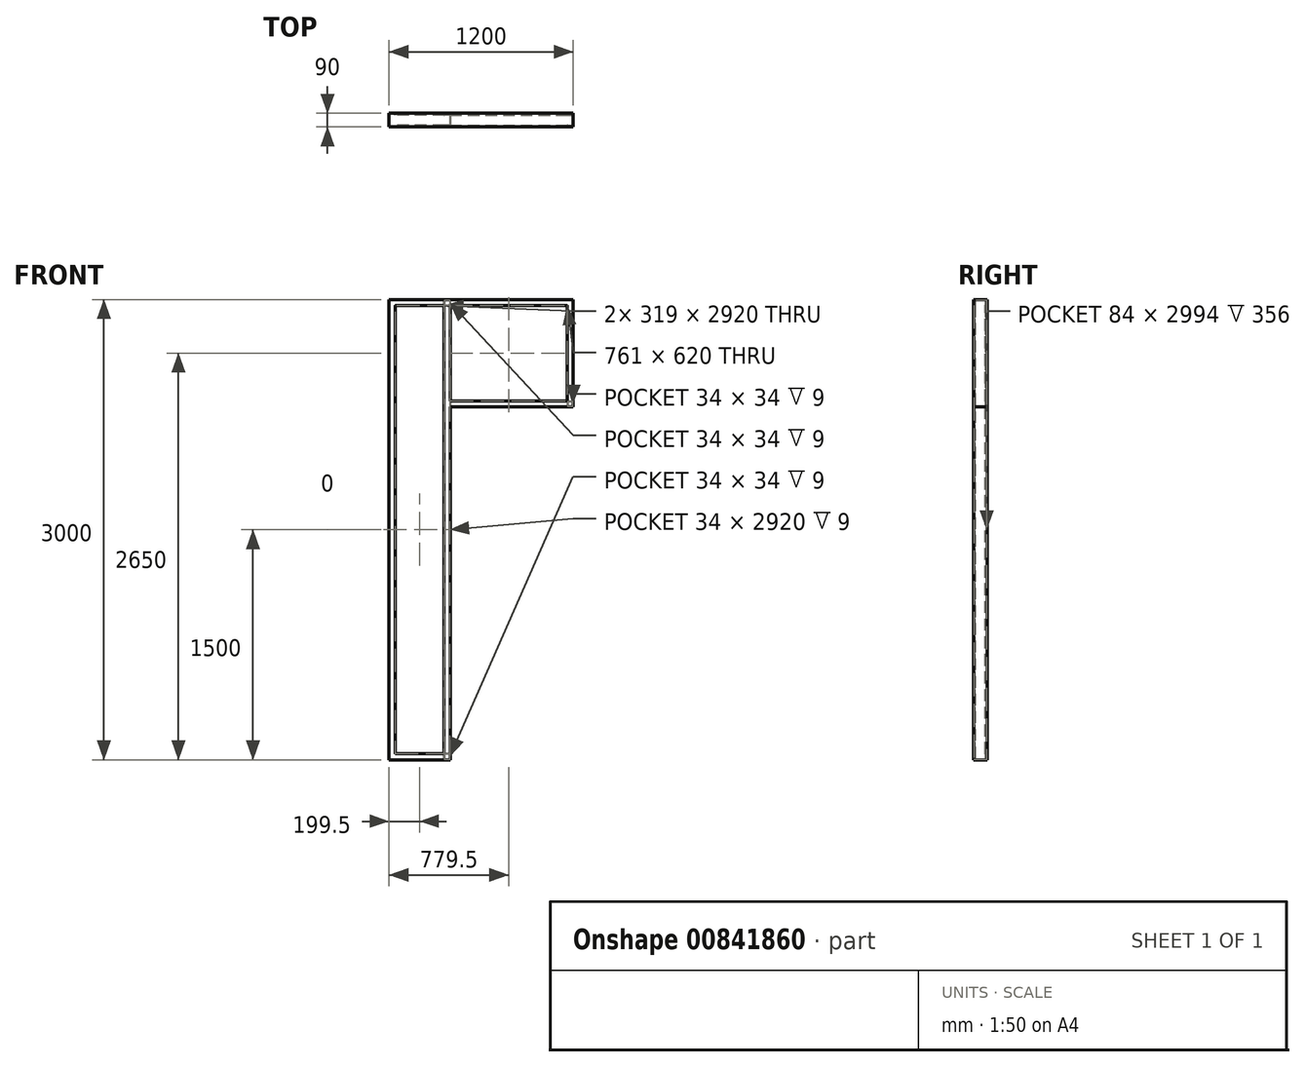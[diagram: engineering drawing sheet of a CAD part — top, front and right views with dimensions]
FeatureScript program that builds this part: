
annotation { "Feature Type Name" : "Feature", "Feature Type Description" : "" }
export const myFeature = defineFeature(function(context is Context, id is Id, definition is map)
    precondition{}
    {
        {
            var Q0;
            Q0=qCreatedBy(makeId("Front.planeOp"),FACE);
            var sketch = newSketch(context, id + "F0", { "sketchPlane" : qUnion([Q0])});
            skLineSegment(sketch, "E0.bottom", {"start": v(0, 0) * mm, "end": v(1200, 0) * mm});
            skLineSegment(sketch, "E0.top", {"start": v(0, 3000) * mm, "end": v(1200, 3000) * mm});
            skLineSegment(sketch, "E0.left", {"start": v(0, 0) * mm, "end": v(0, 3000) * mm});
            skLineSegment(sketch, "E0.right", {"start": v(1200, 0) * mm, "end": v(1200, 3000) * mm});
            skSolve(sketch);
        }
        {
            var Q0;
            Q0=qCreatedBy(makeId("Top.planeOp"),FACE);
            var sketch = newSketch(context, id + "F1", { "sketchPlane" : qUnion([Q0])});
            skLineSegment(sketch, "E1", {"start": v(0, 0) * mm, "end": v(0, -45) * mm});
            skLineSegment(sketch, "E2", {"start": v(0, -45) * mm, "end": v(40, -45) * mm});
            skLineSegment(sketch, "E3", {"start": v(40, -45) * mm, "end": v(40, -33) * mm});
            skLineSegment(sketch, "E4.MirrorCS", {"start": v(0, 0) * mm, "end": v(0, 45) * mm});
            skLineSegment(sketch, "E5.MirrorCS", {"start": v(0, 45) * mm, "end": v(40, 45) * mm});
            skLineSegment(sketch, "E6.MirrorCS", {"start": v(40, 45) * mm, "end": v(40, 33) * mm});
            skLineSegment(sketch, "E7.0", {"start": v(37, 42) * mm, "end": v(37, 33) * mm});
            skLineSegment(sketch, "E7.1", {"start": v(3, 42) * mm, "end": v(37, 42) * mm});
            skLineSegment(sketch, "E7.2", {"start": v(37, -42) * mm, "end": v(37, -33) * mm});
            skLineSegment(sketch, "E7.3", {"start": v(3, -42) * mm, "end": v(37, -42) * mm});
            skLineSegment(sketch, "E7.4", {"start": v(3, 0) * mm, "end": v(3, -42) * mm});
            skLineSegment(sketch, "E7.5", {"start": v(3, 0) * mm, "end": v(3, 42) * mm});
            skLineSegment(sketch, "E8", {"start": v(37, 33) * mm, "end": v(40, 33) * mm});
            skLineSegment(sketch, "E9", {"start": v(37, -33) * mm, "end": v(40, -33) * mm});
            skSolve(sketch);
        }
        {
            var Q0;
            Q0=qSketchRegion(id+"F1",true);
            var Q1;
            Q1=qConstructionFilter(qBodyType(qCreatedBy(id+"F0",EDGE),BodyType.WIRE),ConstructionObject.NO);
            sweep(context, id + "F2", {"profiles" : qUnion([Q0]), "path" : qUnion([Q1])});
        }
        {
            var Q0;
            Q0=qCreatedBy(makeId("Top.planeOp"),FACE);
            var sketch = newSketch(context, id + "F3", { "sketchPlane" : qUnion([Q0])});
            skLineSegment(sketch, "E10", {"start": v(359, -45) * mm, "end": v(399, -45) * mm});
            skLineSegment(sketch, "E11", {"start": v(399, -45) * mm, "end": v(399, 45) * mm});
            skLineSegment(sketch, "E12", {"start": v(399, 45) * mm, "end": v(359, 45) * mm});
            skLineSegment(sketch, "E13", {"start": v(359, 45) * mm, "end": v(359, 33) * mm});
            skLineSegment(sketch, "E14", {"start": v(359, -45) * mm, "end": v(359, -33) * mm});
            skLineSegment(sketch, "E15", {"start": v(400, -276.13) * mm, "end": v(400, 155.47) * mm, "construction": true});
            skLineSegment(sketch, "E16.0", {"start": v(1195, -40) * mm, "end": v(5, -40) * mm});
            skLineSegment(sketch, "E16.1", {"start": v(1195, 40) * mm, "end": v(1195, -40) * mm});
            skLineSegment(sketch, "E16.2", {"start": v(5, 40) * mm, "end": v(1195, 40) * mm});
            skLineSegment(sketch, "E16.3", {"start": v(5, 40) * mm, "end": v(5, -40) * mm});
            skLineSegment(sketch, "E17.0", {"start": v(362, 42) * mm, "end": v(362, 33) * mm});
            skLineSegment(sketch, "E17.1", {"start": v(362, -42) * mm, "end": v(362, -33) * mm});
            skLineSegment(sketch, "E17.2", {"start": v(362, -42) * mm, "end": v(396, -42) * mm});
            skLineSegment(sketch, "E17.3", {"start": v(396, -42) * mm, "end": v(396, 42) * mm});
            skLineSegment(sketch, "E17.4", {"start": v(396, 42) * mm, "end": v(362, 42) * mm});
            skLineSegment(sketch, "E18", {"start": v(362, -33) * mm, "end": v(359, -33) * mm});
            skLineSegment(sketch, "E19", {"start": v(362, 33) * mm, "end": v(359, 33) * mm});
            skSolve(sketch);
        }
        {
            var Q0;
            {var subQ1=sQuery(id+"F3.wireOp",EDGE,"E10");Q0=makeQuery(id+"F3.imprint","IMPRINT",FACE,{"disambiguationData":[TD([[makeQuery(id+"F3.imprint","IMPRINT",EDGE,{"derivedFrom":subQ1}),1.0]])]});}
            var Q1;
            {var subQ0=sQuery(id+"F3.wireOp",EDGE,"E16.0");var subQ1=sQuery(id+"F3.wireOp",EDGE,"E11");var subQ2=makeQuery(id+"F3.imprint","INTERSECT",VERTEX,{"derivedFrom":[subQ1,subQ0]});Q1=makeQuery(id+"F3.imprint","IMPRINT",FACE,{"disambiguationData":[TD([[makeQuery(id+"F3.imprint","IMPRINT",EDGE,{"disambiguationData":[TD([[subQ2,-1.0]])],"derivedFrom":subQ1}),1.0]])]});}
            var Q2;
            {var subQ0=sQuery(id+"F3.wireOp",EDGE,"E18");Q2=makeQuery(id+"F3.imprint","IMPRINT",FACE,{"disambiguationData":[TD([[makeQuery(id+"F3.imprint","IMPRINT",EDGE,{"derivedFrom":subQ0}),1.0]])]});}
            var Q3;
            {var subQ1=sQuery(id+"F3.wireOp",EDGE,"E12");Q3=makeQuery(id+"F3.imprint","IMPRINT",FACE,{"disambiguationData":[TD([[makeQuery(id+"F3.imprint","IMPRINT",EDGE,{"derivedFrom":subQ1}),1.0]])]});}
            var Q4;
            {var subQ0=sQuery(id+"F3.wireOp",EDGE,"E19");Q4=makeQuery(id+"F3.imprint","IMPRINT",FACE,{"disambiguationData":[TD([[makeQuery(id+"F3.imprint","IMPRINT",EDGE,{"derivedFrom":subQ0}),-1.0]])]});}
            var Q5;
            {var subQ0=sQuery(id+"F3.wireOp",EDGE,"fbeb7f0c-a459-400f-91ed-7fec257c8f050.MirrorCS");Q5=makeQuery(id+"F3.imprint","IMPRINT",FACE,{"disambiguationData":[TD([[makeQuery(id+"F3.imprint","IMPRINT",EDGE,{"derivedFrom":subQ0}),1.0]])]});}
            var Q6;
            {var subQ1=sQuery(id+"F3.wireOp",EDGE,"567eaf2c-da89-443f-b3b3-d68592a5250c0.MirrorCS");Q6=makeQuery(id+"F3.imprint","IMPRINT",FACE,{"disambiguationData":[TD([[makeQuery(id+"F3.imprint","IMPRINT",EDGE,{"derivedFrom":subQ1}),-1.0]])]});}
            var Q7;
            {var subQ0=sQuery(id+"F3.wireOp",EDGE,"E16.0");var subQ1=sQuery(id+"F3.wireOp",EDGE,"1e470031-5891-413e-a47c-f06d65b3e17f0.MirrorCS");var subQ2=makeQuery(id+"F3.imprint","INTERSECT",VERTEX,{"derivedFrom":[subQ1,subQ0]});Q7=makeQuery(id+"F3.imprint","IMPRINT",FACE,{"disambiguationData":[TD([[makeQuery(id+"F3.imprint","IMPRINT",EDGE,{"disambiguationData":[TD([[subQ2,-1.0]])],"derivedFrom":subQ1}),-1.0]])]});}
            var Q8;
            {var subQ5=sQuery(id+"F3.wireOp",EDGE,"ca9fbca5-8cf1-4a5b-8b27-837bc25230130.MirrorCS");Q8=makeQuery(id+"F3.imprint","IMPRINT",FACE,{"disambiguationData":[TD([[makeQuery(id+"F3.imprint","IMPRINT",EDGE,{"derivedFrom":subQ5}),-1.0]])]});}
            var Q9;
            {var subQ0=sQuery(id+"F3.wireOp",EDGE,"47aaed49-ff0d-4512-a623-d8c6419a6b470.MirrorCS");Q9=makeQuery(id+"F3.imprint","IMPRINT",FACE,{"disambiguationData":[TD([[makeQuery(id+"F3.imprint","IMPRINT",EDGE,{"derivedFrom":subQ0}),-1.0]])]});}
            var Q10;
            Q10=makeQuery(id+"F2.opSweep","SWEPT_FACE",FACE,{"disambiguationData":[OSD([sQuery(id+"F0.wireOp",EDGE,"E0.top"),sQuery(id+"F1.wireOp",EDGE,"E7.4"),sQuery(id+"F1.wireOp",EDGE,"E7.5")])]});
            extrude(context, id + "F4", {"entities" : qUnion([Q0, Q1, Q2, Q3, Q4, Q5, Q6, Q7, Q8, Q9]), "operationType" : NewBodyOperationType.ADD, "endBound" : BoundingType.UP_TO_SURFACE, "depth" : 25 * mm, "endBoundEntityFace" : qUnion([Q10]), "offsetDistance" : 25 * mm});
        }
        {
            var Q0;
            Q0=makeQuery(id+"F4.boolean.opBoolean","MERGE",FACE,{"derivedFrom":[makeQuery(id+"F2.opSweep","SWEPT_FACE",FACE,{"disambiguationData":[OSD([sQuery(id+"F0.wireOp",EDGE,"E0.left"),sQuery(id+"F1.wireOp",EDGE,"E2")])]}),makeQuery(id+"F4.opExtrude","SWEPT_FACE",FACE,{"disambiguationData":[OSD([sQuery(id+"F3.wireOp",EDGE,"E10")])]})]});
            var sketch = newSketch(context, id + "F5", { "sketchPlane" : qUnion([Q0])});
            skLineSegment(sketch, "E20.bottom", {"start": v(399, 0) * mm, "end": v(1200, 0) * mm});
            skLineSegment(sketch, "E20.top", {"start": v(399, 2300) * mm, "end": v(1200, 2300) * mm});
            skLineSegment(sketch, "E20.left", {"start": v(399, 0) * mm, "end": v(399, 2300) * mm});
            skLineSegment(sketch, "E20.right", {"start": v(1200, 0) * mm, "end": v(1200, 2300) * mm});
            skSolve(sketch);
        }
        {
            var Q0;
            Q0 = qSketchRegion(id + "F5", true);
            extrude(context, id + "F6", {"entities" : qUnion([Q0]), "operationType" : NewBodyOperationType.REMOVE, "endBound" : BoundingType.THROUGH_ALL, "oppositeDirection" : true, "depth" : 25 * mm, "offsetDistance" : 25 * mm});
        }
        {
            var Q0;
            Q0=makeQuery(id+"F2.opSweep","SWEPT_FACE",FACE,{"disambiguationData":[OSD([sQuery(id+"F0.wireOp",EDGE,"E0.right"),sQuery(id+"F1.wireOp",EDGE,"E1"),sQuery(id+"F1.wireOp",EDGE,"E4.MirrorCS")])]});
            var sketch = newSketch(context, id + "F7", { "sketchPlane" : qUnion([Q0])});
            skLineSegment(sketch, "E21", {"start": v(-45, 2340) * mm, "end": v(-45, 2300) * mm});
            skLineSegment(sketch, "E22", {"start": v(-45, 2300) * mm, "end": v(45, 2300) * mm});
            skLineSegment(sketch, "E23", {"start": v(45, 2300) * mm, "end": v(45, 2340) * mm});
            skLineSegment(sketch, "E24", {"start": v(45, 2340) * mm, "end": v(33, 2340) * mm});
            skLineSegment(sketch, "E25", {"start": v(-45, 2340) * mm, "end": v(-33, 2340) * mm});
            skLineSegment(sketch, "E26.0", {"start": v(-42, 2337) * mm, "end": v(-33, 2337) * mm});
            skLineSegment(sketch, "E26.1", {"start": v(42, 2337) * mm, "end": v(33, 2337) * mm});
            skLineSegment(sketch, "E26.2", {"start": v(42, 2303) * mm, "end": v(42, 2337) * mm});
            skLineSegment(sketch, "E26.3", {"start": v(-42, 2303) * mm, "end": v(42, 2303) * mm});
            skLineSegment(sketch, "E26.4", {"start": v(-42, 2337) * mm, "end": v(-42, 2303) * mm});
            skLineSegment(sketch, "E27.0", {"start": v(-40, 2305) * mm, "end": v(40, 2305) * mm});
            skLineSegment(sketch, "E27.1", {"start": v(-40, 2995) * mm, "end": v(-40, 2305) * mm});
            skLineSegment(sketch, "E27.2", {"start": v(40, 2995) * mm, "end": v(-40, 2995) * mm});
            skLineSegment(sketch, "E27.3", {"start": v(40, 2305) * mm, "end": v(40, 2995) * mm});
            skLineSegment(sketch, "E28", {"start": v(-33, 2340) * mm, "end": v(-33, 2337) * mm});
            skLineSegment(sketch, "E29", {"start": v(33, 2340) * mm, "end": v(33, 2337) * mm});
            skSolve(sketch);
        }
        {
            var Q0;
            {var subQ9=sQuery(id+"F7.wireOp",EDGE,"E21");Q0=makeQuery(id+"F7.imprint","IMPRINT",FACE,{"disambiguationData":[TD([[makeQuery(id+"F7.imprint","IMPRINT",EDGE,{"derivedFrom":subQ9}),1.0]])]});}
            var Q1;
            {var subQ0=sQuery(id+"F7.wireOp",EDGE,"E29");Q1=makeQuery(id+"F7.imprint","IMPRINT",FACE,{"disambiguationData":[TD([[makeQuery(id+"F7.imprint","IMPRINT",EDGE,{"derivedFrom":subQ0}),1.0]])]});}
            var Q2;
            {var subQ0=sQuery(id+"F7.wireOp",EDGE,"E28");Q2=makeQuery(id+"F7.imprint","IMPRINT",FACE,{"disambiguationData":[TD([[makeQuery(id+"F7.imprint","IMPRINT",EDGE,{"derivedFrom":subQ0}),-1.0]])]});}
            var Q3;
            Q3=makeQuery(id+"F6.boolean.opBoolean","MERGE",FACE,{"derivedFrom":[makeQuery(id+"F4.opExtrude","SWEPT_FACE",FACE,{"disambiguationData":[OSD([sQuery(id+"F3.wireOp",EDGE,"E11")])]}),makeQuery(id+"F6.opExtrude","SWEPT_FACE",FACE,{"disambiguationData":[OSD([sQuery(id+"F5.wireOp",EDGE,"E20.left")])]})]});
            extrude(context, id + "F8", {"entities" : qUnion([Q0, Q1, Q2]), "operationType" : NewBodyOperationType.ADD, "endBound" : BoundingType.UP_TO_SURFACE, "oppositeDirection" : true, "depth" : 263 * mm, "endBoundEntityFace" : qUnion([Q3]), "offsetDistance" : 25 * mm});
        }
    });
